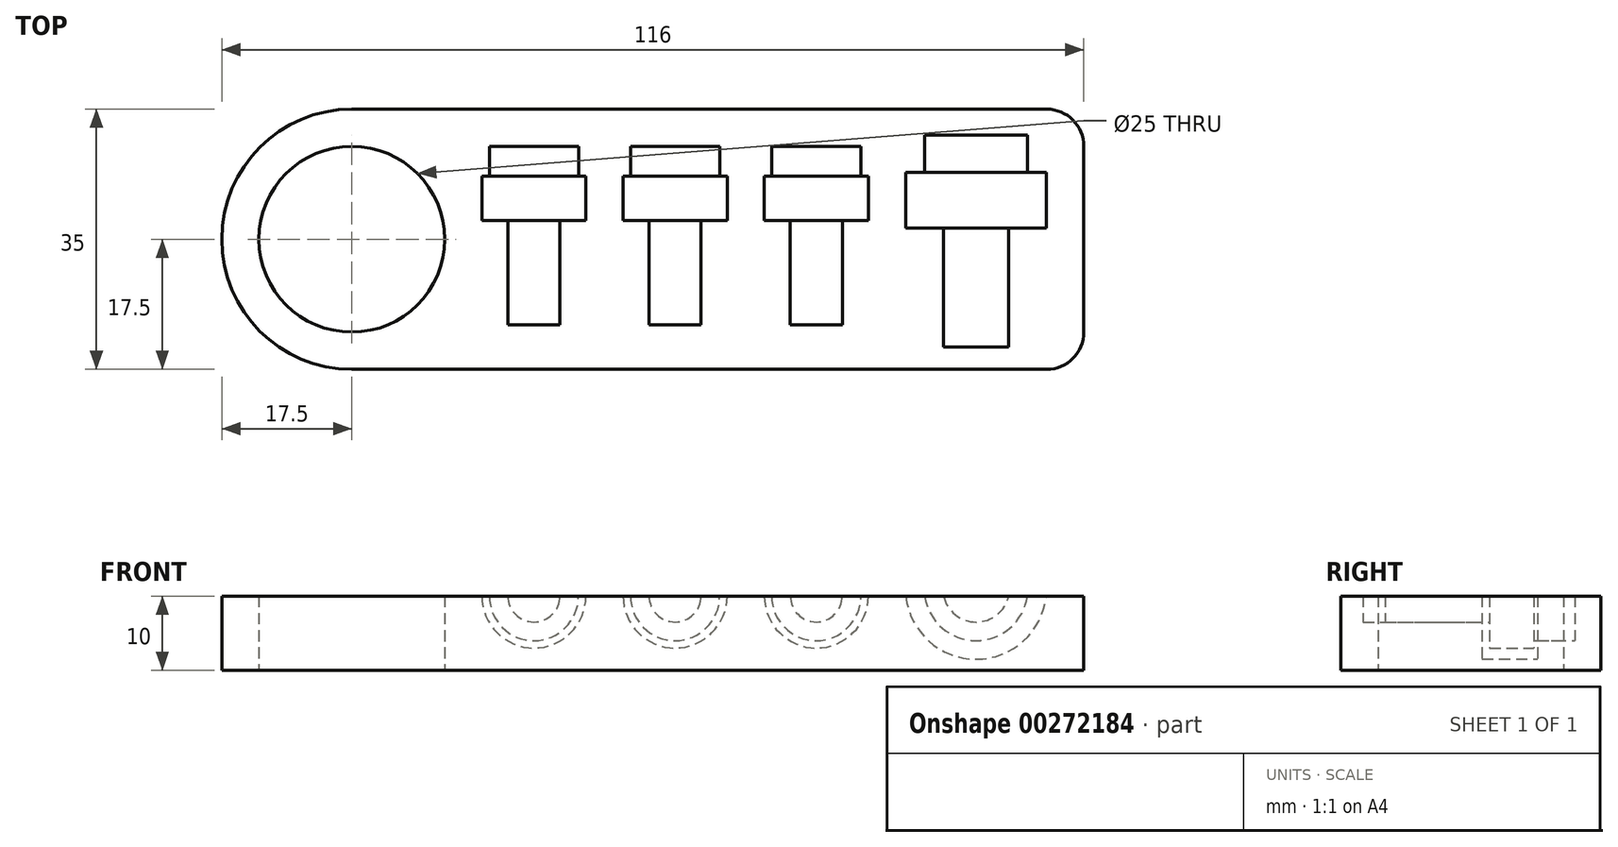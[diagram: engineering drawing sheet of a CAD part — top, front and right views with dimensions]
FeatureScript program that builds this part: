
annotation { "Feature Type Name" : "Feature", "Feature Type Description" : "" }
export const myFeature = defineFeature(function(context is Context, id is Id, definition is map)
    precondition{}
    {
        {
            var Q0;
            Q0=qCreatedBy(makeId("Top.planeOp"),FACE);
            var sketch = newSketch(context, id + "F0", { "sketchPlane" : qUnion([Q0])});
            skLineSegment(sketch, "E0.bottom", {"start": v(17.5, 0) * mm, "end": v(111, 0) * mm});
            skLineSegment(sketch, "E0.top", {"start": v(17.5, 35) * mm, "end": v(111, 35) * mm});
            skLineSegment(sketch, "E0.left", {"start": v(0, 17.5) * mm, "end": v(0, 17.5) * mm});
            skLineSegment(sketch, "E0.right", {"start": v(116, 5) * mm, "end": v(116, 30) * mm});
            skLineSegment(sketch, "E1.bottom", {"start": v(0, 0) * mm, "end": v(17.5, 0) * mm, "construction": true});
            skLineSegment(sketch, "E1.top", {"start": v(0, 17.5) * mm, "end": v(17.5, 17.5) * mm, "construction": true});
            skLineSegment(sketch, "E1.left", {"start": v(0, 0) * mm, "end": v(0, 17.5) * mm, "construction": true});
            skLineSegment(sketch, "E1.right", {"start": v(17.5, 0) * mm, "end": v(17.5, 17.5) * mm, "construction": true});
            skCircle(sketch, "E2", {"center": v(17.5, 17.5) * mm, "radius": 12.5 * mm});
            skPoint(sketch, "E3.visualSharp", {"position": v(0, 0) * mm});
            skArc(sketch, "E3.filletArc", {"start": v(0, 17.5) * mm, "mid": v(5.13, 5.13) * mm, "end": v(17.5, 0) * mm});
            skPoint(sketch, "E4.visualSharp", {"position": v(0, 35) * mm});
            skArc(sketch, "E4.filletArc", {"start": v(17.5, 35) * mm, "mid": v(5.13, 29.87) * mm, "end": v(0, 17.5) * mm});
            skPoint(sketch, "E5.visualSharp", {"position": v(116, 35) * mm});
            skArc(sketch, "E5.filletArc", {"start": v(116, 30) * mm, "mid": v(114.54, 33.54) * mm, "end": v(111, 35) * mm});
            skPoint(sketch, "E6.visualSharp", {"position": v(116, 0) * mm});
            skArc(sketch, "E6.filletArc", {"start": v(111, 0) * mm, "mid": v(114.54, 1.46) * mm, "end": v(116, 5) * mm});
            skSolve(sketch);
        }
        {
            var Q0;
            Q0=makeQuery(id+"F0.imprint","IMPRINT",FACE,{"disambiguationData":[TD([[makeQuery(id+"F0.imprint","IMPRINT",EDGE,{"derivedFrom":sQuery(id+"F0.wireOp",EDGE,"E0.bottom")}),1.0]])]});
            extrude(context, id + "F1", {"entities" : qUnion([Q0]), "depth" : 10 * mm});
        }
        {
            var Q0;
            Q0=makeQuery(id+"F1.opExtrude","CAP_FACE",FACE,{"disambiguationData":[OSD([sQuery(id+"F0.wireOp",EDGE,"E0.bottom"),sQuery(id+"F0.wireOp",EDGE,"E0.top"),sQuery(id+"F0.wireOp",EDGE,"E0.right"),sQuery(id+"F0.wireOp",EDGE,"E2"),sQuery(id+"F0.wireOp",EDGE,"E3.filletArc"),sQuery(id+"F0.wireOp",EDGE,"E4.filletArc"),sQuery(id+"F0.wireOp",EDGE,"E5.filletArc"),sQuery(id+"F0.wireOp",EDGE,"E6.filletArc")])],"isStart":false});
            var sketch = newSketch(context, id + "F2", { "sketchPlane" : qUnion([Q0])});
            skLineSegment(sketch, "E7.bottom", {"start": v(0, 0) * mm, "end": v(42, 0) * mm, "construction": true});
            skLineSegment(sketch, "E7.top", {"start": v(0, 6) * mm, "end": v(42, 6) * mm, "construction": true});
            skLineSegment(sketch, "E7.left", {"start": v(0, 0) * mm, "end": v(0, 6) * mm, "construction": true});
            skLineSegment(sketch, "E7.right", {"start": v(42, 0) * mm, "end": v(42, 6) * mm, "construction": true});
            skLineSegment(sketch, "E8", {"start": v(42, 6) * mm, "end": v(61, 6) * mm, "construction": true});
            skLineSegment(sketch, "E9", {"start": v(61, 6) * mm, "end": v(80, 6) * mm, "construction": true});
            skLineSegment(sketch, "E10.bottom", {"start": v(42, 6) * mm, "end": v(45.5, 6) * mm});
            skLineSegment(sketch, "E10.left", {"start": v(42, 6) * mm, "end": v(42, 20) * mm});
            skLineSegment(sketch, "E10.right", {"start": v(45.5, 6) * mm, "end": v(45.5, 20) * mm});
            skLineSegment(sketch, "E11.bottom", {"start": v(61, 6) * mm, "end": v(64.5, 6) * mm});
            skLineSegment(sketch, "E11.left", {"start": v(61, 6) * mm, "end": v(61, 20) * mm});
            skLineSegment(sketch, "E11.right", {"start": v(64.5, 6) * mm, "end": v(64.5, 20) * mm});
            skLineSegment(sketch, "E12.bottom", {"start": v(80, 6) * mm, "end": v(83.5, 6) * mm});
            skLineSegment(sketch, "E12.left", {"start": v(80, 6) * mm, "end": v(80, 20) * mm});
            skLineSegment(sketch, "E12.right", {"start": v(83.5, 6) * mm, "end": v(83.5, 20) * mm});
            skLineSegment(sketch, "E13.bottom", {"start": v(45.5, 20) * mm, "end": v(49, 20) * mm});
            skLineSegment(sketch, "E13.top", {"start": v(48, 26) * mm, "end": v(49, 26) * mm});
            skLineSegment(sketch, "E13.left", {"start": v(42, 20) * mm, "end": v(42, 26) * mm});
            skLineSegment(sketch, "E13.right", {"start": v(49, 20) * mm, "end": v(49, 26) * mm});
            skLineSegment(sketch, "E14.bottom", {"start": v(64.5, 20) * mm, "end": v(68, 20) * mm});
            skLineSegment(sketch, "E14.top", {"start": v(67, 26) * mm, "end": v(68, 26) * mm});
            skLineSegment(sketch, "E14.left", {"start": v(61, 20) * mm, "end": v(61, 26) * mm});
            skLineSegment(sketch, "E14.right", {"start": v(68, 20) * mm, "end": v(68, 26) * mm});
            skLineSegment(sketch, "E15.bottom", {"start": v(83.5, 20) * mm, "end": v(87, 20) * mm});
            skLineSegment(sketch, "E15.top", {"start": v(86, 26) * mm, "end": v(87, 26) * mm});
            skLineSegment(sketch, "E15.left", {"start": v(80, 20) * mm, "end": v(80, 26) * mm});
            skLineSegment(sketch, "E15.right", {"start": v(87, 20) * mm, "end": v(87, 26) * mm});
            skLineSegment(sketch, "E16.top", {"start": v(42, 30) * mm, "end": v(48, 30) * mm});
            skLineSegment(sketch, "E16.left", {"start": v(42, 26) * mm, "end": v(42, 30) * mm});
            skLineSegment(sketch, "E16.right", {"start": v(48, 26) * mm, "end": v(48, 30) * mm});
            skLineSegment(sketch, "E17.top", {"start": v(61, 30) * mm, "end": v(67, 30) * mm});
            skLineSegment(sketch, "E17.left", {"start": v(61, 26) * mm, "end": v(61, 30) * mm});
            skLineSegment(sketch, "E17.right", {"start": v(67, 26) * mm, "end": v(67, 30) * mm});
            skLineSegment(sketch, "E18.top", {"start": v(80, 30) * mm, "end": v(86, 30) * mm});
            skLineSegment(sketch, "E18.left", {"start": v(80, 26) * mm, "end": v(80, 30) * mm});
            skLineSegment(sketch, "E18.right", {"start": v(86, 26) * mm, "end": v(86, 30) * mm});
            skSolve(sketch);
        }
        {
            var Q0;
            Q0=makeQuery(id+"F2.imprint","IMPRINT",FACE,{"disambiguationData":[TD([[makeQuery(id+"F2.imprint","IMPRINT",EDGE,{"derivedFrom":sQuery(id+"F2.wireOp",EDGE,"E10.bottom")}),1.0]])]});
            var Q1;
            Q1=sQuery(id+"F2.wireOp",EDGE,"E10.left");
            revolve(context, id + "F3", {"operationType" : NewBodyOperationType.REMOVE, "entities" : qUnion([Q0]), "axis" : qUnion([Q1]), "revolveType" : RevolveType.FULL, "oppositeDirection" : true});
        }
        {
            var Q0;
            Q0=makeQuery(id+"F2.imprint","IMPRINT",FACE,{"disambiguationData":[TD([[makeQuery(id+"F2.imprint","IMPRINT",EDGE,{"derivedFrom":sQuery(id+"F2.wireOp",EDGE,"E11.bottom")}),1.0]])]});
            var Q1;
            Q1=sQuery(id+"F2.wireOp",EDGE,"E11.left");
            revolve(context, id + "F4", {"operationType" : NewBodyOperationType.REMOVE, "entities" : qUnion([Q0]), "axis" : qUnion([Q1]), "revolveType" : RevolveType.FULL, "oppositeDirection" : true});
        }
        {
            var Q0;
            Q0=makeQuery(id+"F2.imprint","IMPRINT",FACE,{"disambiguationData":[TD([[makeQuery(id+"F2.imprint","IMPRINT",EDGE,{"derivedFrom":sQuery(id+"F2.wireOp",EDGE,"E12.bottom")}),1.0]])]});
            var Q1;
            Q1=sQuery(id+"F2.wireOp",EDGE,"E12.left");
            revolve(context, id + "F5", {"operationType" : NewBodyOperationType.REMOVE, "entities" : qUnion([Q0]), "axis" : qUnion([Q1]), "revolveType" : RevolveType.FULL, "oppositeDirection" : true});
        }
        {
            var Q0;
            Q0=makeQuery(id+"F1.opExtrude","CAP_FACE",FACE,{"disambiguationData":[OSD([sQuery(id+"F0.wireOp",EDGE,"E0.bottom"),sQuery(id+"F0.wireOp",EDGE,"E0.top"),sQuery(id+"F0.wireOp",EDGE,"E0.right"),sQuery(id+"F0.wireOp",EDGE,"E2"),sQuery(id+"F0.wireOp",EDGE,"E3.filletArc"),sQuery(id+"F0.wireOp",EDGE,"E4.filletArc"),sQuery(id+"F0.wireOp",EDGE,"E5.filletArc"),sQuery(id+"F0.wireOp",EDGE,"E6.filletArc")])],"isStart":false});
            cPlane(context, id + "F6", {"entities" : qUnion([Q0]), "cplaneType" : CPlaneType.OFFSET, "offset" : 1 * mm, "width" : 150 * mm, "height" : 150 * mm});
        }
        {
            var Q0;
            Q0=qCreatedBy(id+"F6.planeOp",FACE);
            var sketch = newSketch(context, id + "F7", { "sketchPlane" : qUnion([Q0])});
            skLineSegment(sketch, "E19.bottom", {"start": v(0, 0) * mm, "end": v(101.5, 0) * mm, "construction": true});
            skLineSegment(sketch, "E19.top", {"start": v(0, 3) * mm, "end": v(101.5, 3) * mm, "construction": true});
            skLineSegment(sketch, "E19.left", {"start": v(0, 0) * mm, "end": v(0, 3) * mm, "construction": true});
            skLineSegment(sketch, "E19.right", {"start": v(101.5, 0) * mm, "end": v(101.5, 3) * mm, "construction": true});
            skLineSegment(sketch, "E20.bottom", {"start": v(101.5, 3) * mm, "end": v(106, 3) * mm});
            skLineSegment(sketch, "E20.left", {"start": v(101.5, 3) * mm, "end": v(101.5, 19) * mm});
            skLineSegment(sketch, "E20.right", {"start": v(106, 3) * mm, "end": v(106, 19) * mm});
            skLineSegment(sketch, "E21.bottom", {"start": v(106, 19) * mm, "end": v(111, 19) * mm});
            skLineSegment(sketch, "E21.top", {"start": v(108.5, 26.5) * mm, "end": v(111, 26.5) * mm});
            skLineSegment(sketch, "E21.left", {"start": v(101.5, 19) * mm, "end": v(101.5, 26.5) * mm});
            skLineSegment(sketch, "E21.right", {"start": v(111, 19) * mm, "end": v(111, 26.5) * mm});
            skLineSegment(sketch, "E22.top", {"start": v(101.5, 31.5) * mm, "end": v(108.5, 31.5) * mm});
            skLineSegment(sketch, "E22.left", {"start": v(101.5, 26.5) * mm, "end": v(101.5, 31.5) * mm});
            skLineSegment(sketch, "E22.right", {"start": v(108.5, 26.5) * mm, "end": v(108.5, 31.5) * mm});
            skSolve(sketch);
        }
        {
            var Q0;
            Q0=makeQuery(id+"F7.imprint","IMPRINT",FACE,{"disambiguationData":[TD([[makeQuery(id+"F7.imprint","IMPRINT",EDGE,{"derivedFrom":sQuery(id+"F7.wireOp",EDGE,"E20.bottom")}),1.0]])]});
            var Q1;
            Q1=sQuery(id+"F7.wireOp",EDGE,"E20.left");
            revolve(context, id + "F8", {"operationType" : NewBodyOperationType.REMOVE, "entities" : qUnion([Q0]), "axis" : qUnion([Q1]), "revolveType" : RevolveType.FULL, "oppositeDirection" : true});
        }
    });
